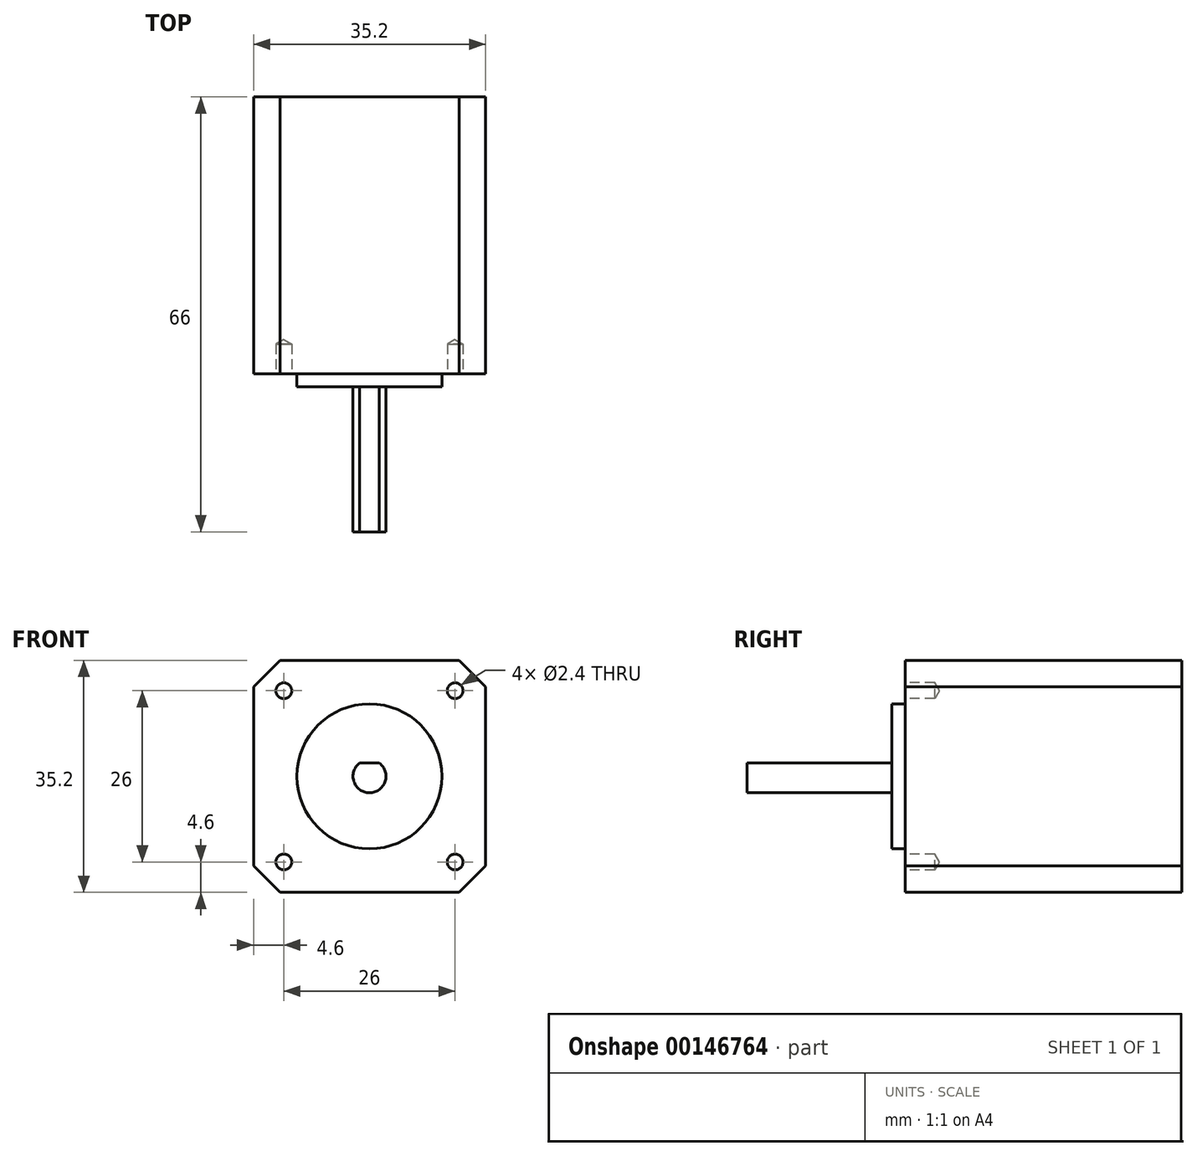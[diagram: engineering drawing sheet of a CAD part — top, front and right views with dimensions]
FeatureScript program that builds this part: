
annotation { "Feature Type Name" : "Feature", "Feature Type Description" : "" }
export const myFeature = defineFeature(function(context is Context, id is Id, definition is map)
    precondition{}
    {
        {
            var Q0;
            Q0=qCreatedBy(makeId("Front.planeOp"),FACE);
            var sketch = newSketch(context, id + "F0", { "sketchPlane" : qUnion([Q0])});
            skLineSegment(sketch, "E0.bottom", {"start": v(17.6, 17.6) * mm, "end": v(-17.6, 17.6) * mm});
            skLineSegment(sketch, "E0.top", {"start": v(17.6, -17.6) * mm, "end": v(-17.6, -17.6) * mm});
            skLineSegment(sketch, "E0.left", {"start": v(17.6, 17.6) * mm, "end": v(17.6, -17.6) * mm});
            skLineSegment(sketch, "E0.right", {"start": v(-17.6, 17.6) * mm, "end": v(-17.6, -17.6) * mm});
            skPoint(sketch, "E0.middle", {"position": v(0, 0) * mm});
            skSolve(sketch);
        }
        {
            var Q0;
            Q0=qSketchRegion(id+"F0",true);
            extrude(context, id + "F1", {"entities" : qUnion([Q0]), "oppositeDirection" : true, "offsetDistance" : 25 * mm, "depth" : 42 * mm});
        }
        {
            var Q0;
            Q0=qCreatedBy(makeId("Front.planeOp"),FACE);
            var sketch = newSketch(context, id + "F2", { "sketchPlane" : qUnion([Q0])});
            skCircle(sketch, "E1", {"center": v(0, 0) * mm, "radius": 11 * mm});
            skSolve(sketch);
        }
        {
            var Q0;
            Q0=qSketchRegion(id+"F2",true);
            extrude(context, id + "F3", {"entities" : qUnion([Q0]), "operationType" : NewBodyOperationType.ADD, "offsetDistance" : 25 * mm, "depth" : 2 * mm});
        }
        {
            var Q0;
            Q0=makeQuery(id+"F3.opExtrude","CAP_FACE",FACE,{"disambiguationData":[OSD([sQuery(id+"F2.wireOp",EDGE,"E1")])],"isStart":false});
            var sketch = newSketch(context, id + "F4", { "sketchPlane" : qUnion([Q0])});
            skArc(sketch, "E2", {"start": v(-1.5, 2) * mm, "mid": v(0, -2.5) * mm, "end": v(1.5, 2) * mm});
            skLineSegment(sketch, "E3", {"start": v(-1.5, 2) * mm, "end": v(1.5, 2) * mm});
            skSolve(sketch);
        }
        {
            var Q0;
            Q0=qSketchRegion(id+"F4",true);
            extrude(context, id + "F5", {"entities" : qUnion([Q0]), "operationType" : NewBodyOperationType.ADD, "offsetDistance" : 25 * mm, "depth" : 22 * mm});
        }
        {
            var Q0;
            Q0=makeQuery(id+"F1.opExtrude","CAP_FACE",FACE,{"disambiguationData":[OSD([sQuery(id+"F0.wireOp",EDGE,"E0.bottom"),sQuery(id+"F0.wireOp",EDGE,"E0.top"),sQuery(id+"F0.wireOp",EDGE,"E0.left"),sQuery(id+"F0.wireOp",EDGE,"E0.right")])],"isStart":true});
            var sketch = newSketch(context, id + "F6", { "sketchPlane" : qUnion([Q0])});
            skLineSegment(sketch, "E4.bottom", {"start": v(13, 13) * mm, "end": v(-13, 13) * mm, "construction": true});
            skLineSegment(sketch, "E4.top", {"start": v(13, -13) * mm, "end": v(-13, -13) * mm, "construction": true});
            skLineSegment(sketch, "E4.left", {"start": v(13, 13) * mm, "end": v(13, -13) * mm, "construction": true});
            skLineSegment(sketch, "E4.right", {"start": v(-13, 13) * mm, "end": v(-13, -13) * mm, "construction": true});
            skPoint(sketch, "E4.middle", {"position": v(0, 0) * mm});
            skSolve(sketch);
        }
        {
            var Q0;
            Q0=sQuery(id+"F6.wireOp",VERTEX,"E4.right.start");
            var Q1;
            Q1=sQuery(id+"F6.wireOp",VERTEX,"E4.left.start");
            var Q2;
            Q2=sQuery(id+"F6.wireOp",VERTEX,"E4.left.end");
            var Q3;
            Q3=sQuery(id+"F6.wireOp",VERTEX,"E4.right.end");
            var Q4;
            Q4=makeQuery(id+"F1.opExtrude","SWEPT_BODY",BODY,{"disambiguationData":[OSD([sQuery(id+"F0.wireOp",EDGE,"E0.bottom"),sQuery(id+"F0.wireOp",EDGE,"E0.top"),sQuery(id+"F0.wireOp",EDGE,"E0.left"),sQuery(id+"F0.wireOp",EDGE,"E0.right")])]});
            hole(context, id + "F7", {"style" : HoleStyle.SIMPLE, "endStyle" : HoleEndStyle.BLIND, "standardTappedOrClearance" : lookupTablePath({ "standard" : "ISO", "engagement" : "75%", "pitch" : "0.6 mm", "size" : "M3", "type" : "Tapped" }), "standardBlindInLast" : lookupTablePath({ "standard" : "ISO", "engagement" : "75%", "pitch" : "0.6 mm", "size" : "M3", "type" : "Tapped" }), "holeDiameter" : 2.4 * mm, "holeDepth" : 4.5 * mm, "locations" : qUnion([Q0, Q1, Q2, Q3]), "scope" : qUnion([Q4])});
        }
        {
            var Q0;
            Q0=makeQuery(id+"F1.opExtrude","SWEPT_EDGE",EDGE,{"disambiguationData":[OSD([sQuery(id+"F0.wireOp",EDGE,"E0.bottom"),sQuery(id+"F0.wireOp",EDGE,"E0.right")])]});
            var Q1;
            Q1=makeQuery(id+"F1.opExtrude","SWEPT_EDGE",EDGE,{"disambiguationData":[OSD([sQuery(id+"F0.wireOp",EDGE,"E0.top"),sQuery(id+"F0.wireOp",EDGE,"E0.right")])]});
            var Q2;
            Q2=makeQuery(id+"F1.opExtrude","SWEPT_EDGE",EDGE,{"disambiguationData":[OSD([sQuery(id+"F0.wireOp",EDGE,"E0.top"),sQuery(id+"F0.wireOp",EDGE,"E0.left")])]});
            var Q3;
            Q3=makeQuery(id+"F1.opExtrude","SWEPT_EDGE",EDGE,{"disambiguationData":[OSD([sQuery(id+"F0.wireOp",EDGE,"E0.bottom"),sQuery(id+"F0.wireOp",EDGE,"E0.left")])]});
            chamfer(context, id + "F8", {"entities" : qUnion([Q0, Q1, Q2, Q3]), "width" : 4 * mm, "tangentPropagation" : true});
        }
    });
